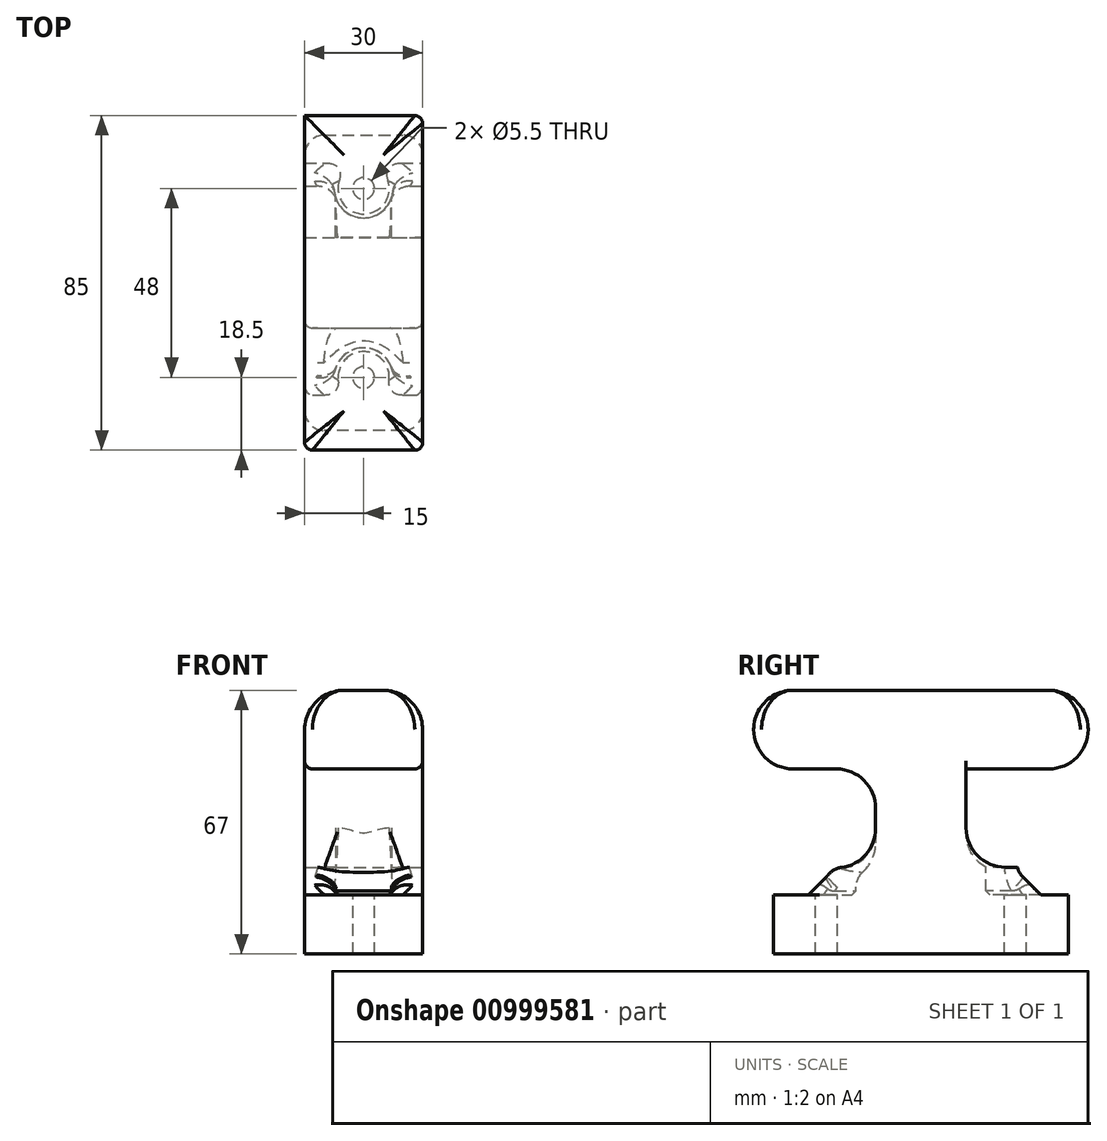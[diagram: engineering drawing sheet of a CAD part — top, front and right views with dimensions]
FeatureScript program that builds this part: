
annotation { "Feature Type Name" : "Feature", "Feature Type Description" : "" }
export const myFeature = defineFeature(function(context is Context, id is Id, definition is map)
    precondition{}
    {
        {
            var Q0;
            Q0=qCreatedBy(makeId("Top.planeOp"),FACE);
            var sketch = newSketch(context, id + "F0", { "sketchPlane" : qUnion([Q0])});
            skLineSegment(sketch, "E0.bottom", {"start": v(0, 0) * mm, "end": v(30, 0) * mm});
            skLineSegment(sketch, "E0.top", {"start": v(0, 75) * mm, "end": v(30, 75) * mm});
            skLineSegment(sketch, "E0.left", {"start": v(0, 0) * mm, "end": v(0, 75) * mm});
            skLineSegment(sketch, "E0.right", {"start": v(30, 0) * mm, "end": v(30, 75) * mm});
            skSolve(sketch);
        }
        {
            var Q0;
            Q0 = qSketchRegion(id + "F0", true);
            extrude(context, id + "F1", {"entities" : qUnion([Q0]), "depth" : 22 * mm, "offsetDistance" : 25 * mm});
        }
        {
            var Q0;
            Q0=makeQuery(id+"F1.opExtrude","CAP_FACE",FACE,{"disambiguationData":[OSD([sQuery(id+"F0.wireOp",EDGE,"E0.bottom"),sQuery(id+"F0.wireOp",EDGE,"E0.top"),sQuery(id+"F0.wireOp",EDGE,"E0.left"),sQuery(id+"F0.wireOp",EDGE,"E0.right")])],"isStart":false});
            var sketch = newSketch(context, id + "F2", { "sketchPlane" : qUnion([Q0])});
            skLineSegment(sketch, "E1", {"start": v(15, 75) * mm, "end": v(15, 0) * mm, "construction": true});
            skLineSegment(sketch, "E2", {"start": v(0, 37.5) * mm, "end": v(30, 37.5) * mm, "construction": true});
            skLineSegment(sketch, "E3", {"start": v(-7.9, 61.5) * mm, "end": v(40.34, 61.5) * mm, "construction": true});
            skLineSegment(sketch, "E4", {"start": v(-9.94, 13.5) * mm, "end": v(43.26, 13.5) * mm, "construction": true});
            skCircle(sketch, "E5", {"center": v(15, 61.5) * mm, "radius": 2.75 * mm});
            skCircle(sketch, "E6", {"center": v(15, 13.5) * mm, "radius": 2.75 * mm});
            skSolve(sketch);
        }
        {
            var Q0;
            Q0 = qSketchRegion(id + "F2", true);
            extrude(context, id + "F3", {"entities" : qUnion([Q0]), "operationType" : NewBodyOperationType.REMOVE, "endBound" : BoundingType.THROUGH_ALL, "oppositeDirection" : true, "depth" : 25 * mm, "offsetDistance" : 25 * mm});
        }
        {
            var Q0;
            Q0=makeQuery(id+"F1.opExtrude","CAP_FACE",FACE,{"disambiguationData":[OSD([sQuery(id+"F0.wireOp",EDGE,"E0.bottom"),sQuery(id+"F0.wireOp",EDGE,"E0.top"),sQuery(id+"F0.wireOp",EDGE,"E0.left"),sQuery(id+"F0.wireOp",EDGE,"E0.right")])],"isStart":false});
            var sketch = newSketch(context, id + "F4", { "sketchPlane" : qUnion([Q0])});
            skCircle(sketch, "E7", {"center": v(15, 61.5) * mm, "radius": 7.5 * mm});
            skCircle(sketch, "E8", {"center": v(15, 13.5) * mm, "radius": 7.5 * mm});
            skSolve(sketch);
        }
        {
            var Q0;
            Q0 = qSketchRegion(id + "F4", true);
            extrude(context, id + "F5", {"entities" : qUnion([Q0]), "operationType" : NewBodyOperationType.REMOVE, "oppositeDirection" : true, "depth" : 7 * mm, "offsetDistance" : 25 * mm});
        }
        {
            var Q0;
            Q0=makeQuery(id+"F1.opExtrude","CAP_FACE",FACE,{"disambiguationData":[OSD([sQuery(id+"F0.wireOp",EDGE,"E0.bottom"),sQuery(id+"F0.wireOp",EDGE,"E0.top"),sQuery(id+"F0.wireOp",EDGE,"E0.left"),sQuery(id+"F0.wireOp",EDGE,"E0.right")])],"isStart":false});
            var sketch = newSketch(context, id + "F6", { "sketchPlane" : qUnion([Q0])});
            skLineSegment(sketch, "E9.bottom", {"start": v(0, 0) * mm, "end": v(30, 0) * mm});
            skLineSegment(sketch, "E9.top", {"start": v(0, 14.83) * mm, "end": v(30, 14.83) * mm});
            skLineSegment(sketch, "E9.left", {"start": v(0, 0) * mm, "end": v(0, 14.83) * mm});
            skLineSegment(sketch, "E9.right", {"start": v(30, 0) * mm, "end": v(30, 14.83) * mm});
            skLineSegment(sketch, "E10.bottom", {"start": v(0, 75) * mm, "end": v(30, 75) * mm});
            skLineSegment(sketch, "E10.top", {"start": v(0, 62.04) * mm, "end": v(30, 62.04) * mm});
            skLineSegment(sketch, "E10.left", {"start": v(0, 75) * mm, "end": v(0, 62.04) * mm});
            skLineSegment(sketch, "E10.right", {"start": v(30, 75) * mm, "end": v(30, 62.04) * mm});
            skSolve(sketch);
        }
        {
            var Q0;
            Q0 = qSketchRegion(id + "F6", true);
            var Q1;
            Q1=makeQuery(id+"F5.boolean.opBoolean","COPY",FACE,{"derivedFrom":makeQuery(id+"F5.opExtrude","CAP_FACE",FACE,{"disambiguationData":[OSD([sQuery(id+"F4.wireOp",EDGE,"E7")])],"isStart":false})});
            extrude(context, id + "F7", {"entities" : qUnion([Q0]), "operationType" : NewBodyOperationType.REMOVE, "endBound" : BoundingType.UP_TO_SURFACE, "oppositeDirection" : true, "depth" : 25 * mm, "endBoundEntityFace" : qUnion([Q1]), "offsetDistance" : 25 * mm});
        }
        {
            var Q0;
            Q0=makeQuery(id+"F5.boolean.opBoolean","COPY",EDGE,{"derivedFrom":makeQuery(id+"F5.opExtrude","CAP_EDGE",EDGE,{"disambiguationData":[OSD([sQuery(id+"F4.wireOp",EDGE,"E7")])],"isStart":false})});
            var Q1;
            Q1=makeQuery(id+"F5.boolean.opBoolean","COPY",EDGE,{"derivedFrom":makeQuery(id+"F5.opExtrude","CAP_EDGE",EDGE,{"disambiguationData":[OSD([sQuery(id+"F4.wireOp",EDGE,"E8")])],"isStart":false})});
            chamfer(context, id + "F8", {"entities" : qUnion([Q0, Q1]), "width" : 1 * mm, "tangentPropagation" : true});
        }
        {
            var Q0;
            {var subQ1=sQuery(id+"F6.wireOp",EDGE,"E10.top");Q0=makeQuery(id+"F7.boolean.opBoolean","COPY",EDGE,{"disambiguationData":[TD([makeQuery(id+"F1.opExtrude","SWEPT_FACE",FACE,{"disambiguationData":[OSD([sQuery(id+"F0.wireOp",EDGE,"E0.left")])]})])],"derivedFrom":makeQuery(id+"F7.opExtrude","CAP_EDGE",EDGE,{"disambiguationData":[OSD([subQ1])],"isStart":false})});}
            var Q1;
            {var subQ0=sQuery(id+"F6.wireOp",EDGE,"E10.top");Q1=makeQuery(id+"F7.boolean.opBoolean","COPY",EDGE,{"disambiguationData":[TD([makeQuery(id+"F1.opExtrude","SWEPT_FACE",FACE,{"disambiguationData":[OSD([sQuery(id+"F0.wireOp",EDGE,"E0.right")])]})])],"derivedFrom":makeQuery(id+"F7.opExtrude","CAP_EDGE",EDGE,{"disambiguationData":[OSD([subQ0])],"isStart":false})});}
            var Q2;
            {var subQ0=sQuery(id+"F6.wireOp",EDGE,"E9.top");Q2=makeQuery(id+"F7.boolean.opBoolean","COPY",EDGE,{"disambiguationData":[TD([makeQuery(id+"F1.opExtrude","SWEPT_FACE",FACE,{"disambiguationData":[OSD([sQuery(id+"F0.wireOp",EDGE,"E0.right")])]})])],"derivedFrom":makeQuery(id+"F7.opExtrude","CAP_EDGE",EDGE,{"disambiguationData":[OSD([subQ0])],"isStart":false})});}
            var Q3;
            {var subQ0=sQuery(id+"F6.wireOp",EDGE,"E9.top");Q3=makeQuery(id+"F7.boolean.opBoolean","COPY",EDGE,{"disambiguationData":[TD([makeQuery(id+"F1.opExtrude","SWEPT_FACE",FACE,{"disambiguationData":[OSD([sQuery(id+"F0.wireOp",EDGE,"E0.left")])]})])],"derivedFrom":makeQuery(id+"F7.opExtrude","CAP_EDGE",EDGE,{"disambiguationData":[OSD([subQ0])],"isStart":false})});}
            chamfer(context, id + "F9", {"entities" : qUnion([Q0, Q1, Q2, Q3]), "width" : 5.9 * mm, "tangentPropagation" : true});
        }
        {
            var Q0;
            {var subQ2=sQuery(id+"F0.wireOp",EDGE,"E0.right");var subQ3=sQuery(id+"F6.wireOp",EDGE,"E9.top");var subQ6=makeQuery(id+"F1.opExtrude","SWEPT_FACE",FACE,{"disambiguationData":[OSD([subQ2])]});var subQ7=makeQuery(id+"F7.opExtrude","SWEPT_FACE",FACE,{"disambiguationData":[OSD([subQ3])]});Q0=makeQuery(id+"F9.opChamfer","BLEND_EDGE",EDGE,{"blendedFrom":[makeQuery(id+"F7.boolean.opBoolean","COPY",EDGE,{"disambiguationData":[TD([subQ6])],"derivedFrom":makeQuery(id+"F7.opExtrude","CAP_EDGE",EDGE,{"disambiguationData":[OSD([subQ3])],"isStart":false})}),makeQuery(id+"F7.boolean.opBoolean","COPY",FACE,{"disambiguationData":[TD([subQ6])],"derivedFrom":subQ7})],"blendedInto":[makeQuery(id+"F7.boolean.opBoolean","COPY",FACE,{"disambiguationData":[TD([subQ6])],"derivedFrom":subQ7})]});}
            var Q1;
            {var subQ2=sQuery(id+"F0.wireOp",EDGE,"E0.left");var subQ3=sQuery(id+"F6.wireOp",EDGE,"E9.top");var subQ6=makeQuery(id+"F1.opExtrude","SWEPT_FACE",FACE,{"disambiguationData":[OSD([subQ2])]});var subQ7=makeQuery(id+"F7.opExtrude","SWEPT_FACE",FACE,{"disambiguationData":[OSD([subQ3])]});Q1=makeQuery(id+"F9.opChamfer","BLEND_EDGE",EDGE,{"blendedFrom":[makeQuery(id+"F7.boolean.opBoolean","COPY",EDGE,{"disambiguationData":[TD([subQ6])],"derivedFrom":makeQuery(id+"F7.opExtrude","CAP_EDGE",EDGE,{"disambiguationData":[OSD([subQ3])],"isStart":false})}),makeQuery(id+"F7.boolean.opBoolean","COPY",FACE,{"disambiguationData":[TD([subQ6])],"derivedFrom":subQ7})],"blendedInto":[makeQuery(id+"F7.boolean.opBoolean","COPY",FACE,{"disambiguationData":[TD([subQ6])],"derivedFrom":subQ7})]});}
            var Q2;
            {var subQ3=sQuery(id+"F0.wireOp",EDGE,"E0.left");var subQ4=makeQuery(id+"F1.opExtrude","SWEPT_FACE",FACE,{"disambiguationData":[OSD([subQ3])]});var subQ5=sQuery(id+"F6.wireOp",EDGE,"E10.top");var subQ7=makeQuery(id+"F7.opExtrude","SWEPT_FACE",FACE,{"disambiguationData":[OSD([subQ5])]});Q2=makeQuery(id+"F9.opChamfer","BLEND_EDGE",EDGE,{"blendedFrom":[makeQuery(id+"F7.boolean.opBoolean","COPY",EDGE,{"disambiguationData":[TD([subQ4])],"derivedFrom":makeQuery(id+"F7.opExtrude","CAP_EDGE",EDGE,{"disambiguationData":[OSD([subQ5])],"isStart":false})}),makeQuery(id+"F7.boolean.opBoolean","COPY",FACE,{"disambiguationData":[TD([subQ4])],"derivedFrom":subQ7})],"blendedInto":[makeQuery(id+"F7.boolean.opBoolean","COPY",FACE,{"disambiguationData":[TD([subQ4])],"derivedFrom":subQ7})]});}
            var Q3;
            {var subQ3=sQuery(id+"F0.wireOp",EDGE,"E0.right");var subQ4=makeQuery(id+"F1.opExtrude","SWEPT_FACE",FACE,{"disambiguationData":[OSD([subQ3])]});var subQ5=sQuery(id+"F6.wireOp",EDGE,"E10.top");var subQ7=makeQuery(id+"F7.opExtrude","SWEPT_FACE",FACE,{"disambiguationData":[OSD([subQ5])]});Q3=makeQuery(id+"F9.opChamfer","BLEND_EDGE",EDGE,{"blendedFrom":[makeQuery(id+"F7.boolean.opBoolean","COPY",EDGE,{"disambiguationData":[TD([subQ4])],"derivedFrom":makeQuery(id+"F7.opExtrude","CAP_EDGE",EDGE,{"disambiguationData":[OSD([subQ5])],"isStart":false})}),makeQuery(id+"F7.boolean.opBoolean","COPY",FACE,{"disambiguationData":[TD([subQ4])],"derivedFrom":subQ7})],"blendedInto":[makeQuery(id+"F7.boolean.opBoolean","COPY",FACE,{"disambiguationData":[TD([subQ4])],"derivedFrom":subQ7})]});}
            fillet(context, id + "F10", {"entities" : qUnion([Q0, Q1, Q2, Q3]), "radius" : 5 * mm, "tangentPropagation" : true, "allowEdgeOverflow" : false});
        }
        {
            var Q0;
            {var subQ0=sQuery(id+"F4.wireOp",EDGE,"E7");var subQ1=makeQuery(id+"F5.boolean.opBoolean","COPY",FACE,{"derivedFrom":makeQuery(id+"F5.opExtrude","SWEPT_FACE",FACE,{"disambiguationData":[OSD([subQ0])]})});var subQ2=sQuery(id+"F6.wireOp",EDGE,"E10.top");Q0=makeQuery(id+"F9.opChamfer","BLEND_EDGE",EDGE,{"blendedFrom":[makeQuery(id+"F7.boolean.opBoolean","COPY",EDGE,{"disambiguationData":[TD([makeQuery(id+"F1.opExtrude","SWEPT_FACE",FACE,{"disambiguationData":[OSD([sQuery(id+"F0.wireOp",EDGE,"E0.left")])]})])],"derivedFrom":makeQuery(id+"F7.opExtrude","CAP_EDGE",EDGE,{"disambiguationData":[OSD([subQ2])],"isStart":false})}),subQ1],"blendedInto":[subQ1]});}
            var Q1;
            {var subQ0=sQuery(id+"F4.wireOp",EDGE,"E7");var subQ1=sQuery(id+"F6.wireOp",EDGE,"E10.top");Q1=makeQuery(id+"F9.opChamfer","BLEND_EDGE",EDGE,{"blendedFrom":[makeQuery(id+"F7.boolean.opBoolean","COPY",EDGE,{"disambiguationData":[TD([makeQuery(id+"F1.opExtrude","SWEPT_FACE",FACE,{"disambiguationData":[OSD([sQuery(id+"F0.wireOp",EDGE,"E0.left")])]})])],"derivedFrom":makeQuery(id+"F7.opExtrude","CAP_EDGE",EDGE,{"disambiguationData":[OSD([subQ1])],"isStart":false})}),makeQuery(id+"F8.opChamfer","BLEND_FACE",FACE,{"disambiguationData":[OSD([subQ0])]})],"blendedInto":[makeQuery(id+"F8.opChamfer","BLEND_FACE",FACE,{"disambiguationData":[OSD([subQ0])]})]});}
            var Q2;
            {var subQ0=sQuery(id+"F4.wireOp",EDGE,"E7");var subQ1=sQuery(id+"F6.wireOp",EDGE,"E10.top");Q2=makeQuery(id+"F9.opChamfer","BLEND_EDGE",EDGE,{"blendedFrom":[makeQuery(id+"F7.boolean.opBoolean","COPY",EDGE,{"disambiguationData":[TD([makeQuery(id+"F1.opExtrude","SWEPT_FACE",FACE,{"disambiguationData":[OSD([sQuery(id+"F0.wireOp",EDGE,"E0.right")])]})])],"derivedFrom":makeQuery(id+"F7.opExtrude","CAP_EDGE",EDGE,{"disambiguationData":[OSD([subQ1])],"isStart":false})}),makeQuery(id+"F8.opChamfer","BLEND_FACE",FACE,{"disambiguationData":[OSD([subQ0])]})],"blendedInto":[makeQuery(id+"F8.opChamfer","BLEND_FACE",FACE,{"disambiguationData":[OSD([subQ0])]})]});}
            var Q3;
            {var subQ0=sQuery(id+"F4.wireOp",EDGE,"E7");var subQ1=makeQuery(id+"F5.boolean.opBoolean","COPY",FACE,{"derivedFrom":makeQuery(id+"F5.opExtrude","SWEPT_FACE",FACE,{"disambiguationData":[OSD([subQ0])]})});var subQ2=sQuery(id+"F6.wireOp",EDGE,"E10.top");Q3=makeQuery(id+"F9.opChamfer","BLEND_EDGE",EDGE,{"blendedFrom":[makeQuery(id+"F7.boolean.opBoolean","COPY",EDGE,{"disambiguationData":[TD([makeQuery(id+"F1.opExtrude","SWEPT_FACE",FACE,{"disambiguationData":[OSD([sQuery(id+"F0.wireOp",EDGE,"E0.right")])]})])],"derivedFrom":makeQuery(id+"F7.opExtrude","CAP_EDGE",EDGE,{"disambiguationData":[OSD([subQ2])],"isStart":false})}),subQ1],"blendedInto":[subQ1]});}
            var Q4;
            {var subQ0=sQuery(id+"F4.wireOp",EDGE,"E8");var subQ1=sQuery(id+"F6.wireOp",EDGE,"E9.top");Q4=makeQuery(id+"F9.opChamfer","BLEND_EDGE",EDGE,{"blendedFrom":[makeQuery(id+"F7.boolean.opBoolean","COPY",EDGE,{"disambiguationData":[TD([makeQuery(id+"F1.opExtrude","SWEPT_FACE",FACE,{"disambiguationData":[OSD([sQuery(id+"F0.wireOp",EDGE,"E0.right")])]})])],"derivedFrom":makeQuery(id+"F7.opExtrude","CAP_EDGE",EDGE,{"disambiguationData":[OSD([subQ1])],"isStart":false})}),makeQuery(id+"F8.opChamfer","BLEND_FACE",FACE,{"disambiguationData":[OSD([subQ0])]})],"blendedInto":[makeQuery(id+"F8.opChamfer","BLEND_FACE",FACE,{"disambiguationData":[OSD([subQ0])]})]});}
            var Q5;
            {var subQ0=sQuery(id+"F4.wireOp",EDGE,"E8");var subQ1=makeQuery(id+"F5.boolean.opBoolean","COPY",FACE,{"derivedFrom":makeQuery(id+"F5.opExtrude","SWEPT_FACE",FACE,{"disambiguationData":[OSD([subQ0])]})});var subQ2=sQuery(id+"F6.wireOp",EDGE,"E9.top");Q5=makeQuery(id+"F9.opChamfer","BLEND_EDGE",EDGE,{"blendedFrom":[makeQuery(id+"F7.boolean.opBoolean","COPY",EDGE,{"disambiguationData":[TD([makeQuery(id+"F1.opExtrude","SWEPT_FACE",FACE,{"disambiguationData":[OSD([sQuery(id+"F0.wireOp",EDGE,"E0.right")])]})])],"derivedFrom":makeQuery(id+"F7.opExtrude","CAP_EDGE",EDGE,{"disambiguationData":[OSD([subQ2])],"isStart":false})}),subQ1],"blendedInto":[subQ1]});}
            var Q6;
            {var subQ0=sQuery(id+"F4.wireOp",EDGE,"E8");var subQ1=makeQuery(id+"F5.boolean.opBoolean","COPY",FACE,{"derivedFrom":makeQuery(id+"F5.opExtrude","SWEPT_FACE",FACE,{"disambiguationData":[OSD([subQ0])]})});var subQ3=sQuery(id+"F0.wireOp",EDGE,"E0.right");var subQ4=sQuery(id+"F6.wireOp",EDGE,"E9.top");var subQ6=makeQuery(id+"F1.opExtrude","SWEPT_FACE",FACE,{"disambiguationData":[OSD([subQ3])]});var subQ7=makeQuery(id+"F7.opExtrude","SWEPT_FACE",FACE,{"disambiguationData":[OSD([subQ4])]});Q6=makeQuery(id+"F10.opFillet","BLEND_EDGE",EDGE,{"blendedFrom":[makeQuery(id+"F9.opChamfer","BLEND_EDGE",EDGE,{"blendedFrom":[makeQuery(id+"F7.boolean.opBoolean","COPY",EDGE,{"disambiguationData":[TD([subQ6])],"derivedFrom":makeQuery(id+"F7.opExtrude","CAP_EDGE",EDGE,{"disambiguationData":[OSD([subQ4])],"isStart":false})}),makeQuery(id+"F7.boolean.opBoolean","COPY",FACE,{"disambiguationData":[TD([subQ6])],"derivedFrom":subQ7})],"blendedInto":[makeQuery(id+"F7.boolean.opBoolean","COPY",FACE,{"disambiguationData":[TD([subQ6])],"derivedFrom":subQ7})]}),subQ1],"blendedInto":[subQ1]});}
            var Q7;
            {var subQ0=sQuery(id+"F4.wireOp",EDGE,"E8");var subQ1=sQuery(id+"F6.wireOp",EDGE,"E9.top");Q7=makeQuery(id+"F9.opChamfer","BLEND_EDGE",EDGE,{"blendedFrom":[makeQuery(id+"F7.boolean.opBoolean","COPY",EDGE,{"disambiguationData":[TD([makeQuery(id+"F1.opExtrude","SWEPT_FACE",FACE,{"disambiguationData":[OSD([sQuery(id+"F0.wireOp",EDGE,"E0.left")])]})])],"derivedFrom":makeQuery(id+"F7.opExtrude","CAP_EDGE",EDGE,{"disambiguationData":[OSD([subQ1])],"isStart":false})}),makeQuery(id+"F8.opChamfer","BLEND_FACE",FACE,{"disambiguationData":[OSD([subQ0])]})],"blendedInto":[makeQuery(id+"F8.opChamfer","BLEND_FACE",FACE,{"disambiguationData":[OSD([subQ0])]})]});}
            var Q8;
            {var subQ0=sQuery(id+"F4.wireOp",EDGE,"E8");var subQ1=makeQuery(id+"F5.boolean.opBoolean","COPY",FACE,{"derivedFrom":makeQuery(id+"F5.opExtrude","SWEPT_FACE",FACE,{"disambiguationData":[OSD([subQ0])]})});var subQ2=sQuery(id+"F6.wireOp",EDGE,"E9.top");Q8=makeQuery(id+"F9.opChamfer","BLEND_EDGE",EDGE,{"blendedFrom":[makeQuery(id+"F7.boolean.opBoolean","COPY",EDGE,{"disambiguationData":[TD([makeQuery(id+"F1.opExtrude","SWEPT_FACE",FACE,{"disambiguationData":[OSD([sQuery(id+"F0.wireOp",EDGE,"E0.left")])]})])],"derivedFrom":makeQuery(id+"F7.opExtrude","CAP_EDGE",EDGE,{"disambiguationData":[OSD([subQ2])],"isStart":false})}),subQ1],"blendedInto":[subQ1]});}
            var Q9;
            {var subQ0=sQuery(id+"F4.wireOp",EDGE,"E8");var subQ1=makeQuery(id+"F5.boolean.opBoolean","COPY",FACE,{"derivedFrom":makeQuery(id+"F5.opExtrude","SWEPT_FACE",FACE,{"disambiguationData":[OSD([subQ0])]})});var subQ3=sQuery(id+"F0.wireOp",EDGE,"E0.left");var subQ4=sQuery(id+"F6.wireOp",EDGE,"E9.top");var subQ6=makeQuery(id+"F1.opExtrude","SWEPT_FACE",FACE,{"disambiguationData":[OSD([subQ3])]});var subQ7=makeQuery(id+"F7.opExtrude","SWEPT_FACE",FACE,{"disambiguationData":[OSD([subQ4])]});Q9=makeQuery(id+"F10.opFillet","BLEND_EDGE",EDGE,{"blendedFrom":[makeQuery(id+"F9.opChamfer","BLEND_EDGE",EDGE,{"blendedFrom":[makeQuery(id+"F7.boolean.opBoolean","COPY",EDGE,{"disambiguationData":[TD([subQ6])],"derivedFrom":makeQuery(id+"F7.opExtrude","CAP_EDGE",EDGE,{"disambiguationData":[OSD([subQ4])],"isStart":false})}),makeQuery(id+"F7.boolean.opBoolean","COPY",FACE,{"disambiguationData":[TD([subQ6])],"derivedFrom":subQ7})],"blendedInto":[makeQuery(id+"F7.boolean.opBoolean","COPY",FACE,{"disambiguationData":[TD([subQ6])],"derivedFrom":subQ7})]}),subQ1],"blendedInto":[subQ1]});}
            fillet(context, id + "F11", {"entities" : qUnion([Q0, Q1, Q2, Q3, Q4, Q5, Q6, Q7, Q8, Q9]), "radius" : 5 * mm, "tangentPropagation" : true, "allowEdgeOverflow" : false});
        }
        {
            var Q0;
            {var subQ0=sQuery(id+"F0.wireOp",EDGE,"E0.left");var subQ1=makeQuery(id+"F1.opExtrude","CAP_FACE",FACE,{"disambiguationData":[OSD([sQuery(id+"F0.wireOp",EDGE,"E0.bottom"),sQuery(id+"F0.wireOp",EDGE,"E0.top"),subQ0,sQuery(id+"F0.wireOp",EDGE,"E0.right")])],"isStart":false});var subQ4=sQuery(id+"F6.wireOp",EDGE,"E9.top");var subQ7=makeQuery(id+"F1.opExtrude","SWEPT_FACE",FACE,{"disambiguationData":[OSD([subQ0])]});var subQ8=makeQuery(id+"F7.opExtrude","SWEPT_FACE",FACE,{"disambiguationData":[OSD([subQ4])]});Q0=makeQuery(id+"F10.opFillet","BLEND_EDGE",EDGE,{"blendedFrom":[makeQuery(id+"F9.opChamfer","BLEND_EDGE",EDGE,{"blendedFrom":[makeQuery(id+"F7.boolean.opBoolean","COPY",EDGE,{"disambiguationData":[TD([subQ7])],"derivedFrom":makeQuery(id+"F7.opExtrude","CAP_EDGE",EDGE,{"disambiguationData":[OSD([subQ4])],"isStart":false})}),makeQuery(id+"F7.boolean.opBoolean","COPY",FACE,{"disambiguationData":[TD([subQ7])],"derivedFrom":subQ8})],"blendedInto":[makeQuery(id+"F7.boolean.opBoolean","COPY",FACE,{"disambiguationData":[TD([subQ7])],"derivedFrom":subQ8})]}),subQ1],"blendedInto":[subQ1]});}
            var Q1;
            Q1=makeQuery(id+"F5.boolean.opBoolean","COPY",EDGE,{"derivedFrom":makeQuery(id+"F5.opExtrude","CAP_EDGE",EDGE,{"disambiguationData":[OSD([sQuery(id+"F4.wireOp",EDGE,"E7")])],"isStart":true})});
            fillet(context, id + "F12", {"entities" : qUnion([Q0, Q1]), "radius" : 5 * mm, "tangentPropagation" : true, "allowEdgeOverflow" : false});
        }
        {
            var Q0;
            Q0=makeQuery(id+"F1.opExtrude","CAP_FACE",FACE,{"disambiguationData":[OSD([sQuery(id+"F0.wireOp",EDGE,"E0.bottom"),sQuery(id+"F0.wireOp",EDGE,"E0.top"),sQuery(id+"F0.wireOp",EDGE,"E0.left"),sQuery(id+"F0.wireOp",EDGE,"E0.right")])],"isStart":false});
            var sketch = newSketch(context, id + "F13", { "sketchPlane" : qUnion([Q0])});
            skPoint(sketch, "E11.firstSnap0", {"position": v(15, 26) * mm});
            skPoint(sketch, "E11.oppositeSnap0", {"position": v(15, 49) * mm});
            skLineSegment(sketch, "E11.bottom", {"start": v(0, 26) * mm, "end": v(30, 26) * mm});
            skLineSegment(sketch, "E11.top", {"start": v(0, 49) * mm, "end": v(30, 49) * mm});
            skLineSegment(sketch, "E11.left", {"start": v(0, 26) * mm, "end": v(0, 49) * mm});
            skLineSegment(sketch, "E11.right", {"start": v(30, 26) * mm, "end": v(30, 49) * mm});
            skSolve(sketch);
        }
        {
            var Q0;
            Q0 = qSketchRegion(id + "F13", true);
            extrude(context, id + "F14", {"entities" : qUnion([Q0]), "operationType" : NewBodyOperationType.ADD, "depth" : 25 * mm, "offsetDistance" : 25 * mm});
        }
        {
            var Q0;
            Q0=makeQuery(id+"F1.opExtrude","SWEPT_EDGE",EDGE,{"disambiguationData":[OSD([sQuery(id+"F0.wireOp",EDGE,"E0.bottom"),sQuery(id+"F0.wireOp",EDGE,"E0.right")])]});
            var Q1;
            Q1=makeQuery(id+"F1.opExtrude","SWEPT_EDGE",EDGE,{"disambiguationData":[OSD([sQuery(id+"F0.wireOp",EDGE,"E0.bottom"),sQuery(id+"F0.wireOp",EDGE,"E0.left")])]});
            var Q2;
            Q2=makeQuery(id+"F1.opExtrude","SWEPT_EDGE",EDGE,{"disambiguationData":[OSD([sQuery(id+"F0.wireOp",EDGE,"E0.top"),sQuery(id+"F0.wireOp",EDGE,"E0.right")])]});
            var Q3;
            Q3=makeQuery(id+"F1.opExtrude","SWEPT_EDGE",EDGE,{"disambiguationData":[OSD([sQuery(id+"F0.wireOp",EDGE,"E0.top"),sQuery(id+"F0.wireOp",EDGE,"E0.left")])]});
            fillet(context, id + "F15", {"entities" : qUnion([Q0, Q1, Q2, Q3]), "radius" : 5 * mm, "tangentPropagation" : true, "allowEdgeOverflow" : false});
        }
        {
            var Q0;
            Q0=makeQuery(id+"F14.opExtrude","CAP_FACE",FACE,{"disambiguationData":[OSD([sQuery(id+"F13.wireOp",EDGE,"E11.bottom"),sQuery(id+"F13.wireOp",EDGE,"E11.top"),sQuery(id+"F13.wireOp",EDGE,"E11.left"),sQuery(id+"F13.wireOp",EDGE,"E11.right")])],"isStart":false});
            var sketch = newSketch(context, id + "F16", { "sketchPlane" : qUnion([Q0])});
            skLineSegment(sketch, "E12", {"start": v(0, 37.5) * mm, "end": v(60.97, 37.5) * mm, "construction": true});
            skLineSegment(sketch, "E13", {"start": v(-22.07, 80) * mm, "end": v(76.1, 80) * mm, "construction": true});
            skLineSegment(sketch, "E14", {"start": v(-22.58, -5) * mm, "end": v(107.88, -5) * mm, "construction": true});
            skPoint(sketch, "E15.endSnap0", {"position": v(15, 26) * mm});
            skLineSegment(sketch, "E16.bottom", {"start": v(0, 80) * mm, "end": v(30, 80) * mm});
            skLineSegment(sketch, "E16.top", {"start": v(0, -5) * mm, "end": v(30, -5) * mm});
            skLineSegment(sketch, "E16.left", {"start": v(0, 80) * mm, "end": v(0, -5) * mm});
            skLineSegment(sketch, "E16.right", {"start": v(30, 80) * mm, "end": v(30, -5) * mm});
            skSolve(sketch);
        }
        {
            var Q0;
            Q0 = qSketchRegion(id + "F16", true);
            extrude(context, id + "F17", {"entities" : qUnion([Q0]), "operationType" : NewBodyOperationType.ADD, "depth" : 20 * mm, "offsetDistance" : 25 * mm});
        }
        {
            var Q0;
            Q0=makeQuery(id+"F14.opExtrude","CAP_EDGE",EDGE,{"disambiguationData":[OSD([sQuery(id+"F13.wireOp",EDGE,"E11.bottom")])],"isStart":false});
            var Q1;
            {var subQ0=sQuery(id+"F13.wireOp",EDGE,"E11.bottom");var subQ1=sQuery(id+"F0.wireOp",EDGE,"E0.left");Q1=makeQuery(id+"F14.boolean.opBoolean","SPLIT",EDGE,{"disambiguationData":[TD([makeQuery(id+"F1.opExtrude","SWEPT_FACE",FACE,{"disambiguationData":[OSD([subQ1])]})])],"derivedFrom":makeQuery(id+"F14.opExtrude","CAP_EDGE",EDGE,{"disambiguationData":[OSD([subQ0])],"isStart":true})});}
            var Q2;
            Q2=makeQuery(id+"F14.opExtrude","CAP_EDGE",EDGE,{"disambiguationData":[OSD([sQuery(id+"F13.wireOp",EDGE,"E11.top")])],"isStart":false});
            var Q3;
            {var subQ0=sQuery(id+"F13.wireOp",EDGE,"E11.top");var subQ1=sQuery(id+"F0.wireOp",EDGE,"E0.left");Q3=makeQuery(id+"F14.boolean.opBoolean","SPLIT",EDGE,{"disambiguationData":[TD([makeQuery(id+"F1.opExtrude","SWEPT_FACE",FACE,{"disambiguationData":[OSD([subQ1])]})])],"derivedFrom":makeQuery(id+"F14.opExtrude","CAP_EDGE",EDGE,{"disambiguationData":[OSD([subQ0])],"isStart":true})});}
            var Q4;
            Q4=makeQuery(id+"F17.opExtrude","CAP_EDGE",EDGE,{"disambiguationData":[OSD([sQuery(id+"F16.wireOp",EDGE,"E16.bottom")])],"isStart":true});
            var Q5;
            Q5=makeQuery(id+"F17.opExtrude","CAP_EDGE",EDGE,{"disambiguationData":[OSD([sQuery(id+"F16.wireOp",EDGE,"E16.bottom")])],"isStart":false});
            var Q6;
            Q6=makeQuery(id+"F17.opExtrude","CAP_EDGE",EDGE,{"disambiguationData":[OSD([sQuery(id+"F16.wireOp",EDGE,"E16.top")])],"isStart":false});
            var Q7;
            Q7=makeQuery(id+"F17.opExtrude","CAP_EDGE",EDGE,{"disambiguationData":[OSD([sQuery(id+"F16.wireOp",EDGE,"E16.top")])],"isStart":true});
            var Q8;
            Q8=makeQuery(id+"F7.boolean.opBoolean","COPY",EDGE,{"derivedFrom":makeQuery(id+"F7.opExtrude","CAP_EDGE",EDGE,{"disambiguationData":[OSD([sQuery(id+"F6.wireOp",EDGE,"E9.bottom")])],"isStart":false})});
            var Q9;
            Q9=makeQuery(id+"F7.boolean.opBoolean","COPY",EDGE,{"derivedFrom":makeQuery(id+"F7.opExtrude","CAP_EDGE",EDGE,{"disambiguationData":[OSD([sQuery(id+"F6.wireOp",EDGE,"E10.bottom")])],"isStart":false})});
            var Q10;
            Q10=makeQuery(id+"F17.opExtrude","CAP_EDGE",EDGE,{"disambiguationData":[OSD([sQuery(id+"F16.wireOp",EDGE,"E16.right")])],"isStart":false});
            var Q11;
            Q11=makeQuery(id+"F17.opExtrude","CAP_EDGE",EDGE,{"disambiguationData":[OSD([sQuery(id+"F16.wireOp",EDGE,"E16.left")])],"isStart":false});
            fillet(context, id + "F18", {"entities" : qUnion([Q0, Q1, Q2, Q3, Q4, Q5, Q6, Q7, Q8, Q9, Q10, Q11]), "radius" : 10 * mm, "tangentPropagation" : true, "allowEdgeOverflow" : false});
        }
        {
            var Q0;
            {var subQ0=sQuery(id+"F16.wireOp",EDGE,"E16.left");Q0=makeQuery(id+"F17.boolean.opBoolean","SPLIT",EDGE,{"disambiguationData":[TD([makeQuery(id+"F14.opExtrude","SWEPT_FACE",FACE,{"disambiguationData":[OSD([sQuery(id+"F13.wireOp",EDGE,"E11.bottom")])]})])],"derivedFrom":makeQuery(id+"F17.opExtrude","CAP_EDGE",EDGE,{"disambiguationData":[OSD([subQ0])],"isStart":true})});}
            var Q1;
            Q1=makeQuery(id+"F18.opFillet","BLEND_EDGE",EDGE,{"blendedFrom":[makeQuery(id+"F14.opExtrude","CAP_EDGE",EDGE,{"disambiguationData":[OSD([sQuery(id+"F13.wireOp",EDGE,"E11.top")])],"isStart":false}),makeQuery(id+"F17.boolean.opBoolean","MERGE",FACE,{"derivedFrom":[makeQuery(id+"F14.boolean.opBoolean","MERGE",FACE,{"derivedFrom":[makeQuery(id+"F1.opExtrude","SWEPT_FACE",FACE,{"disambiguationData":[OSD([sQuery(id+"F0.wireOp",EDGE,"E0.left")])]}),makeQuery(id+"F14.opExtrude","SWEPT_FACE",FACE,{"disambiguationData":[OSD([sQuery(id+"F13.wireOp",EDGE,"E11.left")])]})]}),makeQuery(id+"F17.opExtrude","SWEPT_FACE",FACE,{"disambiguationData":[OSD([sQuery(id+"F16.wireOp",EDGE,"E16.left")])]})]})],"blendedInto":[makeQuery(id+"F17.boolean.opBoolean","MERGE",FACE,{"derivedFrom":[makeQuery(id+"F14.boolean.opBoolean","MERGE",FACE,{"derivedFrom":[makeQuery(id+"F1.opExtrude","SWEPT_FACE",FACE,{"disambiguationData":[OSD([sQuery(id+"F0.wireOp",EDGE,"E0.left")])]}),makeQuery(id+"F14.opExtrude","SWEPT_FACE",FACE,{"disambiguationData":[OSD([sQuery(id+"F13.wireOp",EDGE,"E11.left")])]})]}),makeQuery(id+"F17.opExtrude","SWEPT_FACE",FACE,{"disambiguationData":[OSD([sQuery(id+"F16.wireOp",EDGE,"E16.left")])]})]})]});
            var Q2;
            Q2=makeQuery(id+"F18.opFillet","BLEND_EDGE",EDGE,{"blendedFrom":[makeQuery(id+"F17.opExtrude","CAP_EDGE",EDGE,{"disambiguationData":[OSD([sQuery(id+"F16.wireOp",EDGE,"E16.bottom")])],"isStart":true}),makeQuery(id+"F17.boolean.opBoolean","MERGE",FACE,{"derivedFrom":[makeQuery(id+"F14.boolean.opBoolean","MERGE",FACE,{"derivedFrom":[makeQuery(id+"F1.opExtrude","SWEPT_FACE",FACE,{"disambiguationData":[OSD([sQuery(id+"F0.wireOp",EDGE,"E0.right")])]}),makeQuery(id+"F14.opExtrude","SWEPT_FACE",FACE,{"disambiguationData":[OSD([sQuery(id+"F13.wireOp",EDGE,"E11.right")])]})]}),makeQuery(id+"F17.opExtrude","SWEPT_FACE",FACE,{"disambiguationData":[OSD([sQuery(id+"F16.wireOp",EDGE,"E16.right")])]})]})],"blendedInto":[makeQuery(id+"F17.boolean.opBoolean","MERGE",FACE,{"derivedFrom":[makeQuery(id+"F14.boolean.opBoolean","MERGE",FACE,{"derivedFrom":[makeQuery(id+"F1.opExtrude","SWEPT_FACE",FACE,{"disambiguationData":[OSD([sQuery(id+"F0.wireOp",EDGE,"E0.right")])]}),makeQuery(id+"F14.opExtrude","SWEPT_FACE",FACE,{"disambiguationData":[OSD([sQuery(id+"F13.wireOp",EDGE,"E11.right")])]})]}),makeQuery(id+"F17.opExtrude","SWEPT_FACE",FACE,{"disambiguationData":[OSD([sQuery(id+"F16.wireOp",EDGE,"E16.right")])]})]})]});
            var Q3;
            Q3=makeQuery(id+"F18.opFillet","BLEND_EDGE",EDGE,{"blendedFrom":[makeQuery(id+"F17.opExtrude","CAP_EDGE",EDGE,{"disambiguationData":[OSD([sQuery(id+"F16.wireOp",EDGE,"E16.top")])],"isStart":true}),makeQuery(id+"F17.boolean.opBoolean","MERGE",FACE,{"derivedFrom":[makeQuery(id+"F14.boolean.opBoolean","MERGE",FACE,{"derivedFrom":[makeQuery(id+"F1.opExtrude","SWEPT_FACE",FACE,{"disambiguationData":[OSD([sQuery(id+"F0.wireOp",EDGE,"E0.right")])]}),makeQuery(id+"F14.opExtrude","SWEPT_FACE",FACE,{"disambiguationData":[OSD([sQuery(id+"F13.wireOp",EDGE,"E11.right")])]})]}),makeQuery(id+"F17.opExtrude","SWEPT_FACE",FACE,{"disambiguationData":[OSD([sQuery(id+"F16.wireOp",EDGE,"E16.right")])]})]})],"blendedInto":[makeQuery(id+"F17.boolean.opBoolean","MERGE",FACE,{"derivedFrom":[makeQuery(id+"F14.boolean.opBoolean","MERGE",FACE,{"derivedFrom":[makeQuery(id+"F1.opExtrude","SWEPT_FACE",FACE,{"disambiguationData":[OSD([sQuery(id+"F0.wireOp",EDGE,"E0.right")])]}),makeQuery(id+"F14.opExtrude","SWEPT_FACE",FACE,{"disambiguationData":[OSD([sQuery(id+"F13.wireOp",EDGE,"E11.right")])]})]}),makeQuery(id+"F17.opExtrude","SWEPT_FACE",FACE,{"disambiguationData":[OSD([sQuery(id+"F16.wireOp",EDGE,"E16.right")])]})]})]});
            fillet(context, id + "F19", {"entities" : qUnion([Q0, Q1, Q2, Q3]), "radius" : 2 * mm, "tangentPropagation" : true, "allowEdgeOverflow" : false});
        }
    });
